# Revit family: E-949
name_source: partatom
category: Plumbing Fixtures
units: mm (PartAtom-declared; Revit-internal decimal feet)

## family parameters
Always vertical = Yes
Cut with Voids When Loaded = No
OmniClass Number = 23.45.00.00
OmniClass Title = Sanitary, Laundry, and Cleaning Equipment
Part Type = Normal
Room Calculation Point = No
Round Connector Dimension = Use Diameter
Shared = Yes
Work Plane-Based = Yes

## types (2) — shared parameters
Accesorios = Contra de Push, Inserto para Rebosadero, Herramienta de Sujeción, Llave para Aireador, Llave para Mantenimiento, Llave Allen 5/64".
Anchura Total = 4"
Características del Producto = Monomando para lavabo con desagüe de push.
Cartucho = Cartucho Ø25 mm con vástago metálico.
Cuerpo de Latón = Brass
Default Elevation = 35"
Garantía = El producto HELVEX está garantizado como libre de defectos en materiales y procesos de fabricación. El producto HELVEX está garantizado, en lo que se refiere a los acabados; por un periodo de 10 años en los acabados cromo y duravex, y por 2 años en acabados diferentes al cromo, a partir de la fecha de compra indicada en la factura.
Guía de Instalación = http://www.helvex.com
Instalación = Conexión ½ - 14 NPSM
Manufacturer = HELVEX S.A. de C.V.
Model = E-948
Operación = Levante el maneral para abrir el flujo y gire a la derecha para más fría o a la izquierda para más caliente.
Presión Máxima de Trabajo = 85.3 psi
Presión Mínima de Trabajo = 8.5 psi
Profundidad Total = 7"
URL = https://www.helvex.com.mx

## per-type parameters (varying)
| type | Altura Total | Description | Ficha Técnica | Type Comments | Type Image |
| E-924 | 6" | Monomando Legorreta E-948 | http://www.helvex.com | Monomando para Lavabo con Desagüe de Push | <None> |
| E-949 | 11" | Monomando Legorreta Alto E-949 | https://www.helvex.com.mx | Monomando Alto para Lavabo con Desague de Push | E-949.jpg |

## geometry (parser evidence)
native form markers: Sweep x3
no freeform markers — native parametric forms only
